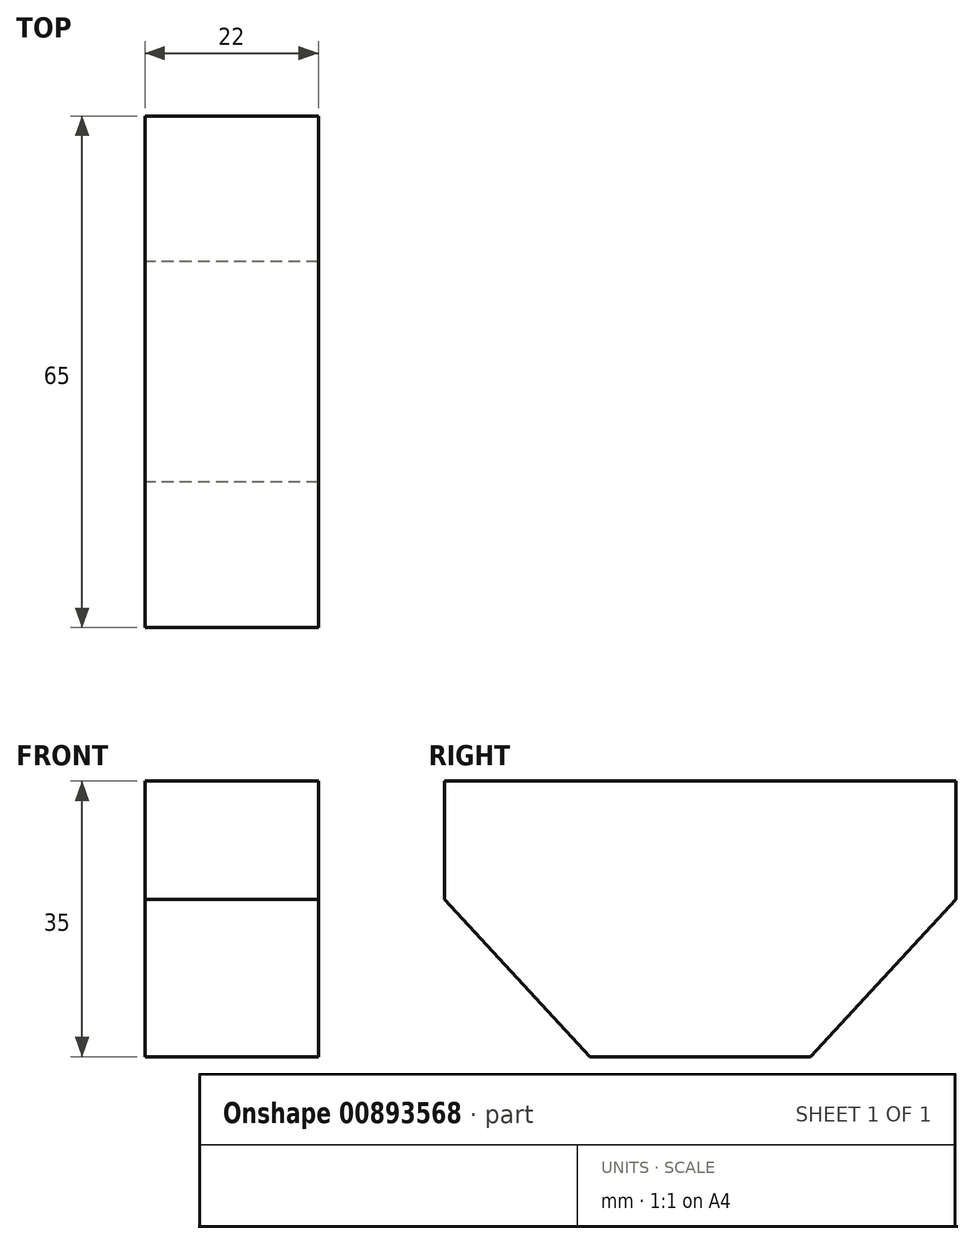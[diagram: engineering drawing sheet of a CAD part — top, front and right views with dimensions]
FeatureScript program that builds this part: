
annotation { "Feature Type Name" : "Feature", "Feature Type Description" : "" }
export const myFeature = defineFeature(function(context is Context, id is Id, definition is map)
    precondition{}
    {
        {
            var Q0;
            Q0=qCreatedBy(makeId("Right.planeOp"),FACE);
            var sketch = newSketch(context, id + "F0", { "sketchPlane" : qUnion([Q0])});
            skLineSegment(sketch, "E0", {"start": v(0, 0) * mm, "end": v(32.5, 0) * mm});
            skLineSegment(sketch, "E1", {"start": v(32.5, 0) * mm, "end": v(32.5, -15) * mm});
            skLineSegment(sketch, "E2", {"start": v(32.5, -15) * mm, "end": v(14, -35) * mm});
            skLineSegment(sketch, "E3", {"start": v(14, -35) * mm, "end": v(0, -35) * mm});
            skLineSegment(sketch, "E4", {"start": v(0, 0) * mm, "end": v(0, -35) * mm});
            skLineSegment(sketch, "E5.MirrorCS", {"start": v(0, 0) * mm, "end": v(-32.5, 0) * mm});
            skLineSegment(sketch, "E6.MirrorCS", {"start": v(-32.5, 0) * mm, "end": v(-32.5, -15) * mm});
            skLineSegment(sketch, "E7.MirrorCS", {"start": v(-32.5, -15) * mm, "end": v(-14, -35) * mm});
            skLineSegment(sketch, "E8.MirrorCS", {"start": v(-14, -35) * mm, "end": v(0, -35) * mm});
            skSolve(sketch);
        }
        {
            var Q0;
            Q0 = qSketchRegion(id + "F0", true);
            extrude(context, id + "F1", {"entities" : qUnion([Q0]), "depth" : 22 * mm, "offsetDistance" : 25.4 * mm});
        }
    });
